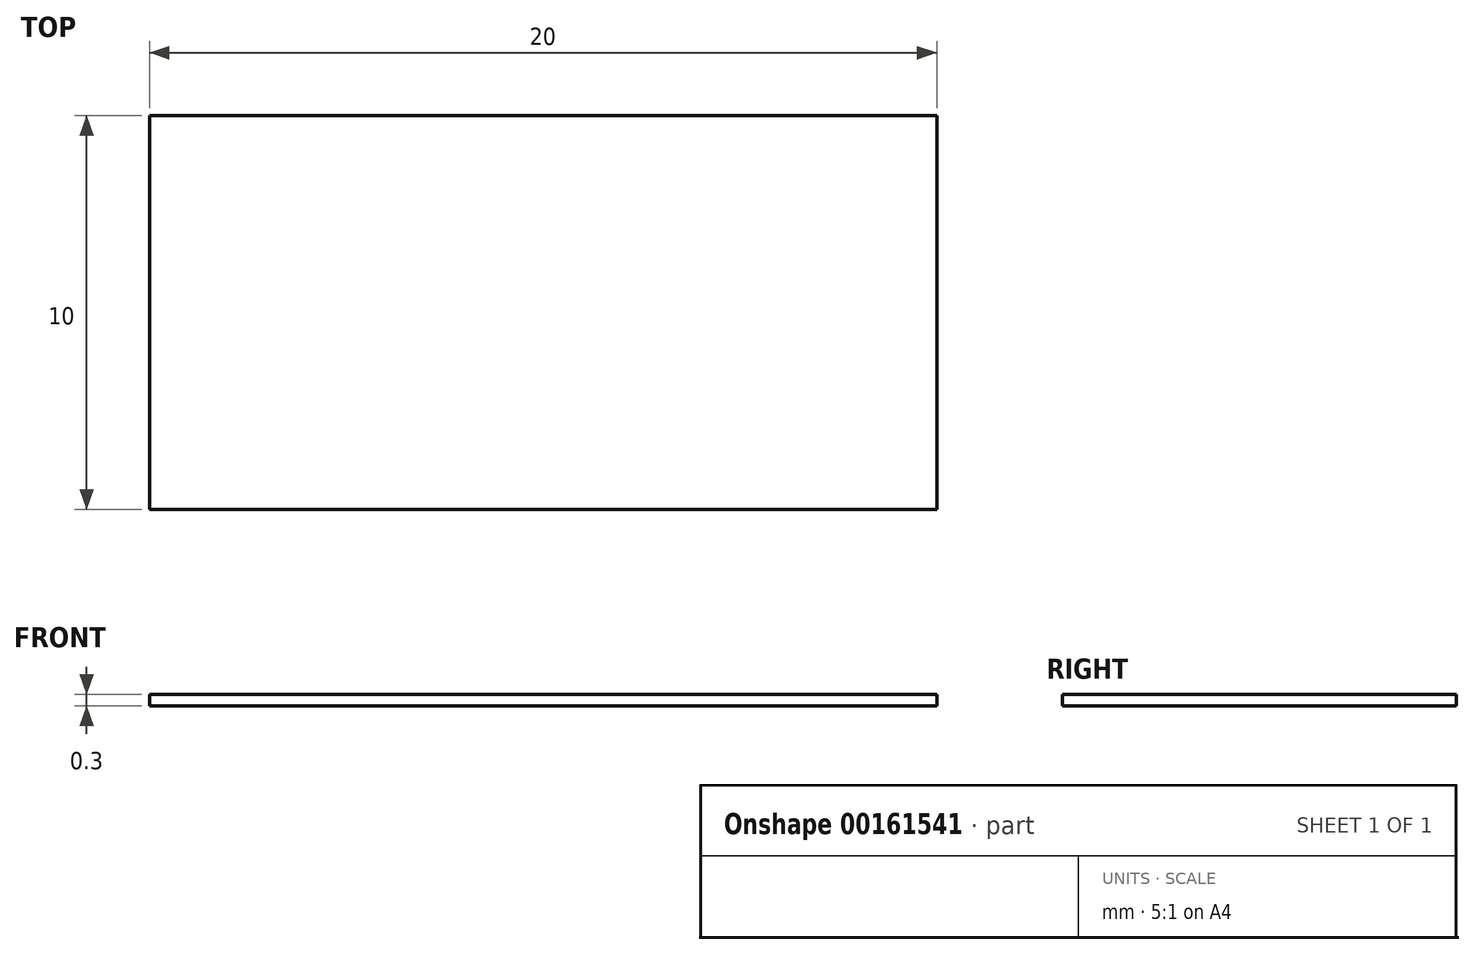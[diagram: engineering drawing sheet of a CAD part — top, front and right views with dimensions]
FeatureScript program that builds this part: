
annotation { "Feature Type Name" : "Feature", "Feature Type Description" : "" }
export const myFeature = defineFeature(function(context is Context, id is Id, definition is map)
    precondition{}
    {
        {
            var Q0;
            Q0=qCreatedBy(makeId("Top.planeOp"),FACE);
            var sketch = newSketch(context, id + "F0", { "sketchPlane" : qUnion([Q0])});
            skLineSegment(sketch, "E0.bottom", {"start": v(10, 5) * mm, "end": v(-10, 5) * mm});
            skLineSegment(sketch, "E0.top", {"start": v(10, -5) * mm, "end": v(-10, -5) * mm});
            skLineSegment(sketch, "E0.left", {"start": v(10, 5) * mm, "end": v(10, -5) * mm});
            skLineSegment(sketch, "E0.right", {"start": v(-10, 5) * mm, "end": v(-10, -5) * mm});
            skPoint(sketch, "E0.middle", {"position": v(0, 0) * mm});
            skSolve(sketch);
        }
        {
            var Q0;
            Q0 = qSketchRegion(id + "F0", true);
            var Q1;
            Q1 = qConstructionFilter(qBodyType(qCreatedBy(id + "F0" ,EDGE), BodyType.WIRE), ConstructionObject.NO);
            extrude(context, id + "F1", {"entities" : qUnion([Q0]), "surfaceEntities" : qUnion([Q1]), "depth" : .3 * mm});
        }
    });
